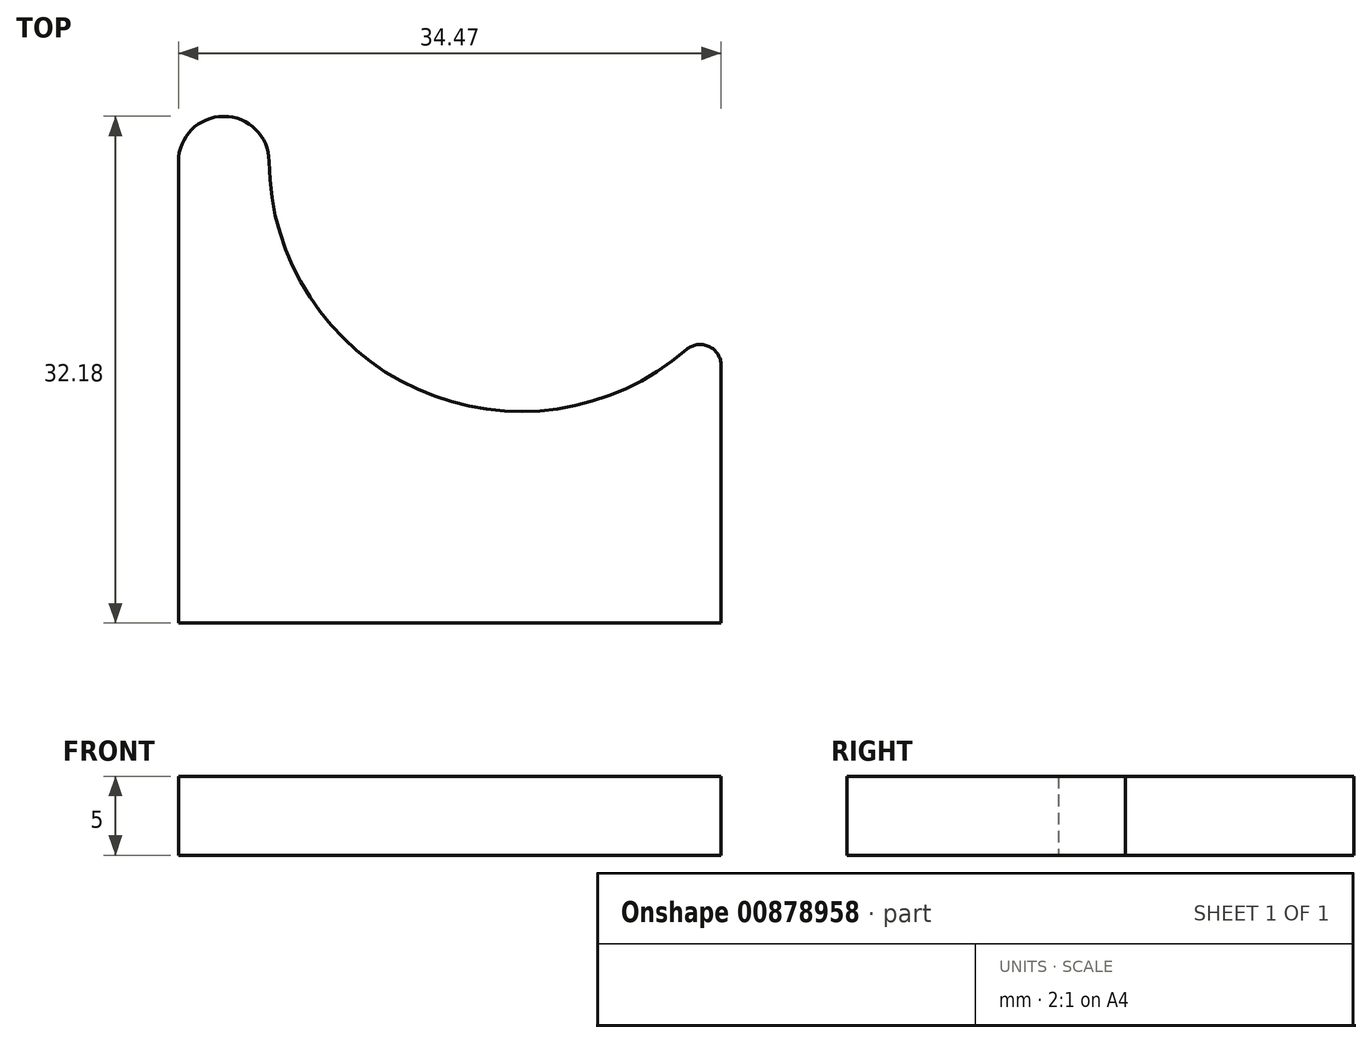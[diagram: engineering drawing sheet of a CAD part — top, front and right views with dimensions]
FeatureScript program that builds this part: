
annotation { "Feature Type Name" : "Feature", "Feature Type Description" : "" }
export const myFeature = defineFeature(function(context is Context, id is Id, definition is map)
    precondition{}
    {
        {
            var Q0;
            Q0=qCreatedBy(makeId("Top.planeOp"),FACE);
            var sketch = newSketch(context, id + "F0", { "sketchPlane" : qUnion([Q0])});
            skLineSegment(sketch, "E0.bottom", {"start": v(0, 0) * mm, "end": v(34.47, 0) * mm});
            skLineSegment(sketch, "E0.left", {"start": v(0, 0) * mm, "end": v(0, 29.3) * mm});
            skLineSegment(sketch, "E0.right", {"start": v(34.47, 0) * mm, "end": v(34.47, 16.35) * mm});
            skArc(sketch, "E1", {"start": v(5.76, 29.32) * mm, "mid": v(15.17, 14.85) * mm, "end": v(32.26, 17.36) * mm});
            skCircle(sketch, "E2", {"center": v(33.13, 16.35) * mm, "radius": 1.34 * mm});
            skCircle(sketch, "E3", {"center": v(2.88, 29.3) * mm, "radius": 2.88 * mm});
            skSolve(sketch);
        }
        {
            var Q0;
            Q0=qSketchRegion(id+"F0",true);
            extrude(context, id + "F1", {"entities" : qUnion([Q0]), "depth" : 5 * mm, "offsetDistance" : 25 * mm});
        }
        {
            var Q0;
            Q0=makeQuery(id+"F1.opExtrude","CAP_FACE",FACE,{"disambiguationData":[OSD([sQuery(id+"F0.wireOp",EDGE,"E0.bottom"),sQuery(id+"F0.wireOp",EDGE,"E0.left"),sQuery(id+"F0.wireOp",EDGE,"E0.right"),sQuery(id+"F0.wireOp",EDGE,"E1"),sQuery(id+"F0.wireOp",EDGE,"E2"),sQuery(id+"F0.wireOp",EDGE,"E3")])],"isStart":false});
            var sketch = newSketch(context, id + "F2", { "sketchPlane" : qUnion([Q0])});
            skSolve(sketch);
        }
        {
            var Q0;
            {var subQ0=makeQuery(id+"F1.opExtrude","CAP_EDGE",EDGE,{"disambiguationData":[OSD([sQuery(id+"F0.wireOp",EDGE,"E0.bottom")])],"isStart":false});Q0=makeQuery(id+"F2.imprint","IMPRINT",FACE,{"disambiguationData":[TD([[makeQuery(id+"F2.imprint","IMPRINT",EDGE,{"derivedFrom":subQ0}),1.0]])]});}
            var Q1;
            Q1=makeQuery(id+"F2.imprint","IMPRINT",FACE,{"disambiguationData":[TD([[makeQuery(id+"F2.imprint","IMPRINT",EDGE,{"derivedFrom":sQuery(id+"F2.wireOp",EDGE,"zG1yROjU-JeBR-3h8o-1pPd-KSsYQ7IM8QkO")}),-1.0]])]});
            var Q2;
            {var subQ0=sQuery(id+"F2.wireOp",EDGE,"irv26uyZ-Q05m-Obbf-i6gP-vnwM5PRfqptf");Q2=makeQuery(id+"F2.imprint","IMPRINT",FACE,{"disambiguationData":[TD([[makeQuery(id+"F2.imprint","IMPRINT",EDGE,{"derivedFrom":subQ0}),-1.0]])]});}
            var Q3;
            Q3=makeQuery(id+"F2.imprint","IMPRINT",FACE,{"disambiguationData":[TD([[makeQuery(id+"F2.imprint","IMPRINT",EDGE,{"derivedFrom":sQuery(id+"F2.wireOp",EDGE,"2BshW728-1PGd-FBAO-OUDW-M6yzmwUXOPcH")}),1.0]])]});
            extrude(context, id + "F3", {"entities" : qUnion([Q0, Q1, Q2, Q3]), "operationType" : NewBodyOperationType.ADD, "oppositeDirection" : true, "depth" : 5 * mm, "offsetDistance" : 25 * mm});
        }
    });
